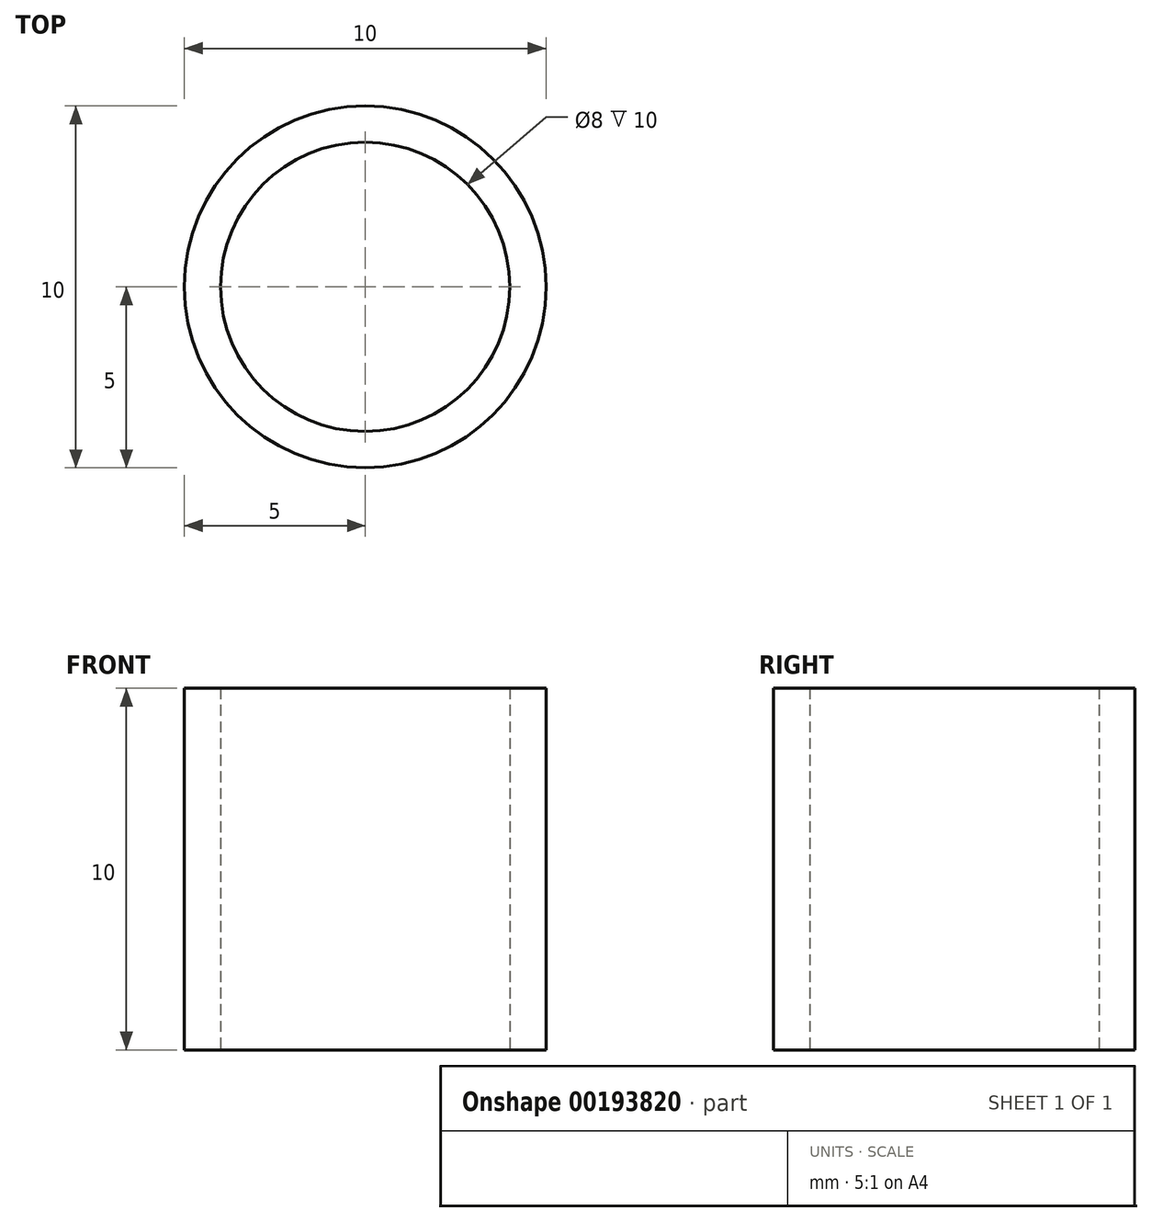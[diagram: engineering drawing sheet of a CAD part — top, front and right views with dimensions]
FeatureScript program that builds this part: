
annotation { "Feature Type Name" : "Feature", "Feature Type Description" : "" }
export const myFeature = defineFeature(function(context is Context, id is Id, definition is map)
    precondition{}
    {
        {
            var Q0;
            Q0=qCreatedBy(makeId("Top.planeOp"),FACE);
            var sketch = newSketch(context, id + "F0", { "sketchPlane" : qUnion([Q0])});
            skCircle(sketch, "E0", {"center": v(0, 0) * mm, "radius": 5 * mm});
            skCircle(sketch, "E1.0", {"center": v(0, 0) * mm, "radius": 4 * mm});
            skSolve(sketch);
        }
        {
            var Q0;
            Q0=makeQuery(id+"F0.imprint","IMPRINT",FACE,{"disambiguationData":[TD([[makeQuery(id+"F0.imprint","IMPRINT",EDGE,{"derivedFrom":sQuery(id+"F0.wireOp",EDGE,"E0")}),1.0]])]});
            extrude(context, id + "F1", {"entities" : qUnion([Q0]), "depth" : 10 * mm});
        }
    });
